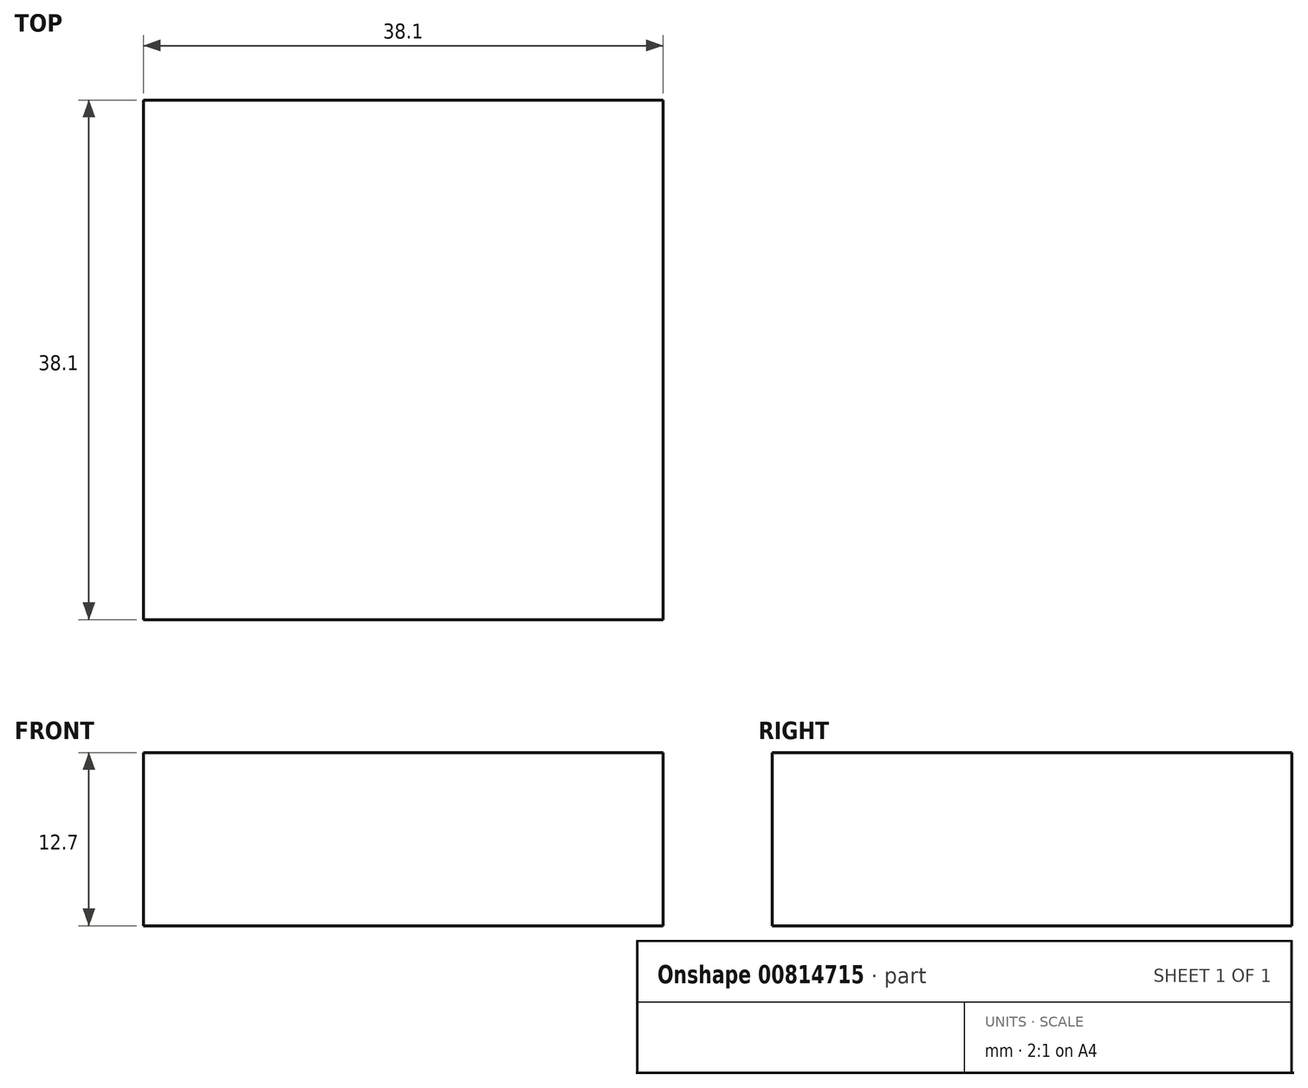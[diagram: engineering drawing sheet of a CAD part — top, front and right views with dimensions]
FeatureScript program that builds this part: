
annotation { "Feature Type Name" : "Feature", "Feature Type Description" : "" }
export const myFeature = defineFeature(function(context is Context, id is Id, definition is map)
    precondition{}
    {
        {
            var Q0;
            Q0=qCreatedBy(makeId("Front.planeOp"),FACE);
            var sketch = newSketch(context, id + "F0", { "sketchPlane" : qUnion([Q0])});
            skLineSegment(sketch, "E0", {"start": v(0, 0) * mm, "end": v(38.1, 0) * mm});
            skLineSegment(sketch, "E1", {"start": v(38.1, 0) * mm, "end": v(38.1, 12.7) * mm});
            skLineSegment(sketch, "E2", {"start": v(38.1, 12.7) * mm, "end": v(0, 12.7) * mm});
            skLineSegment(sketch, "E3", {"start": v(0, 12.7) * mm, "end": v(0, 0) * mm});
            skSolve(sketch);
        }
        {
            var Q0;
            Q0 = qSketchRegion(id + "F0", true);
            extrude(context, id + "F1", {"entities" : qUnion([Q0]), "depth" : 38.1 * mm, "offsetDistance" : 25.4 * mm});
        }
    });
